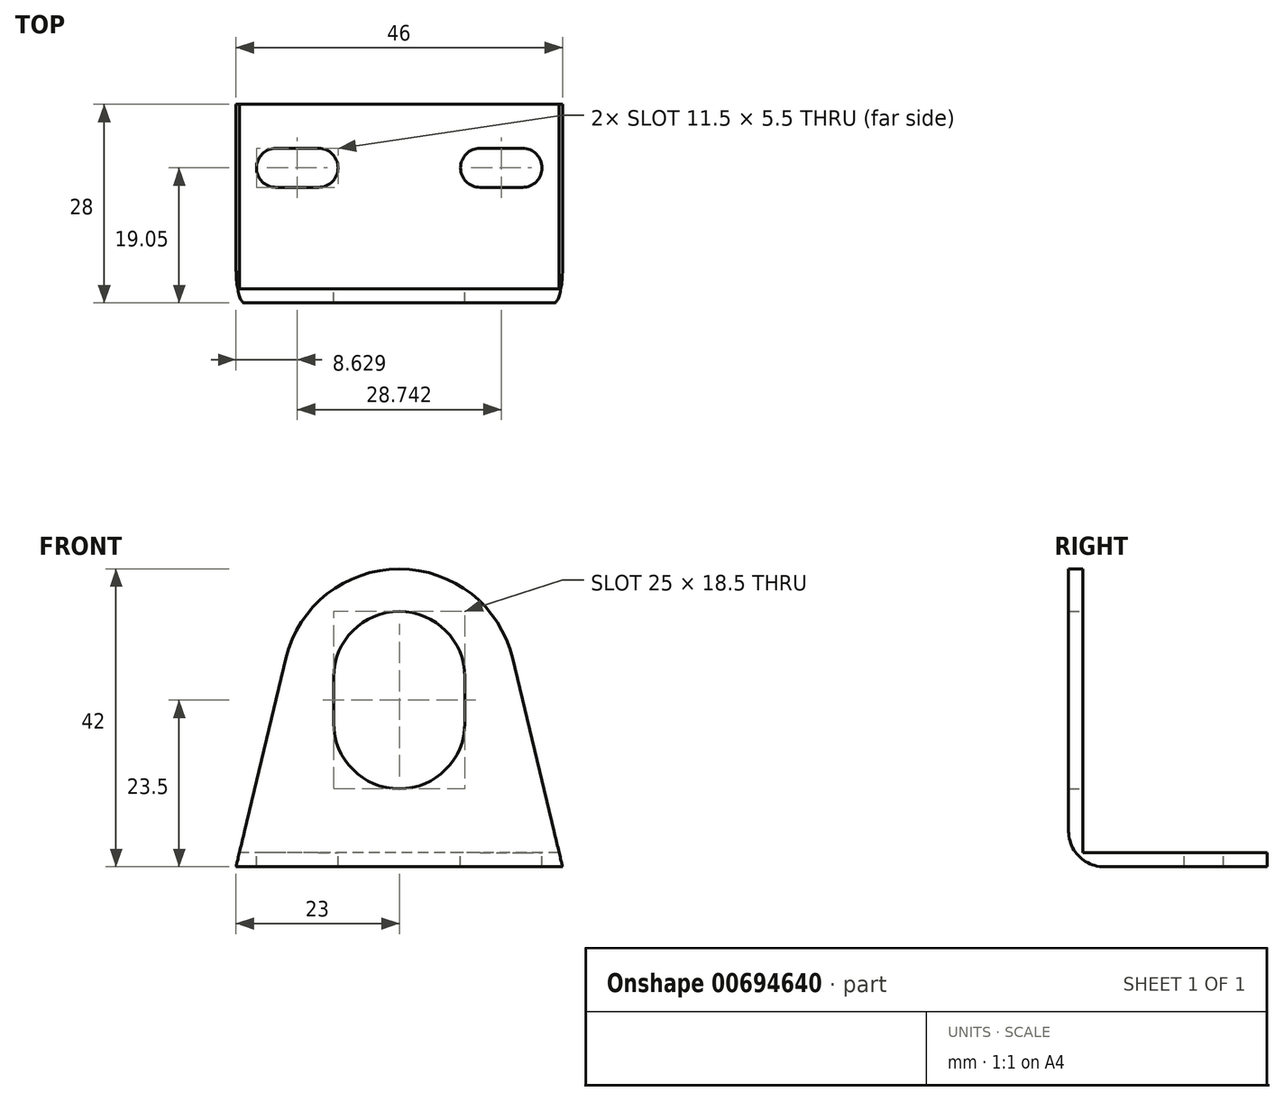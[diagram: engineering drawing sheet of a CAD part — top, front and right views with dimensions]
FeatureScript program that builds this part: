
annotation { "Feature Type Name" : "Feature", "Feature Type Description" : "" }
export const myFeature = defineFeature(function(context is Context, id is Id, definition is map)
    precondition{}
    {
        {
            var Q0;
            Q0=qCreatedBy(makeId("Front.planeOp"),FACE);
            var sketch = newSketch(context, id + "F0", { "sketchPlane" : qUnion([Q0])});
            skLineSegment(sketch, "E0", {"start": v(-23, 0) * mm, "end": v(23, 0) * mm});
            skLineSegment(sketch, "E1", {"start": v(23, 0) * mm, "end": v(15.96, 29.41) * mm});
            skLineSegment(sketch, "E2", {"start": v(-23, 0) * mm, "end": v(-15.96, 29.41) * mm});
            skArc(sketch, "E3", {"start": v(15.96, 29.41) * mm, "mid": v(0, 42) * mm, "end": v(-15.96, 29.41) * mm});
            skLineSegment(sketch, "E4", {"start": v(-9.25, 26.75) * mm, "end": v(-9.25, 20.25) * mm});
            skLineSegment(sketch, "E5", {"start": v(9.25, 26.75) * mm, "end": v(9.25, 20.25) * mm});
            skArc(sketch, "E6", {"start": v(-9.25, 20.25) * mm, "mid": v(0, 11) * mm, "end": v(9.25, 20.25) * mm});
            skArc(sketch, "E7", {"start": v(9.25, 26.75) * mm, "mid": v(0, 36) * mm, "end": v(-9.25, 26.75) * mm});
            skPoint(sketch, "E8", {"position": v(0, 0) * mm});
            skPoint(sketch, "E9", {"position": v(0, 42) * mm});
            skSolve(sketch);
        }
        {
            var Q0;
            Q0=qSketchRegion(id+"F0",true);
            extrude(context, id + "F1", {"entities" : qUnion([Q0]), "depth" : 2 * mm, "offsetDistance" : 25 * mm});
        }
        {
            var Q0;
            Q0=makeQuery(id+"F1.opExtrude","CAP_FACE",FACE,{"disambiguationData":[OSD([sQuery(id+"F0.wireOp",EDGE,"E0"),sQuery(id+"F0.wireOp",EDGE,"E1"),sQuery(id+"F0.wireOp",EDGE,"E2"),sQuery(id+"F0.wireOp",EDGE,"E3"),sQuery(id+"F0.wireOp",EDGE,"E4"),sQuery(id+"F0.wireOp",EDGE,"E5"),sQuery(id+"F0.wireOp",EDGE,"E6"),sQuery(id+"F0.wireOp",EDGE,"E7")])],"isStart":true});
            var sketch = newSketch(context, id + "F2", { "sketchPlane" : qUnion([Q0])});
            skLineSegment(sketch, "E10", {"start": v(-22.52, 2) * mm, "end": v(22.52, 2) * mm});
            skSolve(sketch);
        }
        {
            var Q0;
            {var subQ0=sQuery(id+"F2.wireOp",EDGE,"E10");Q0=makeQuery(id+"F2.imprint","IMPRINT",FACE,{"disambiguationData":[TD([[makeQuery(id+"F2.imprint","IMPRINT",EDGE,{"derivedFrom":subQ0}),-1.0]])]});}
            extrude(context, id + "F3", {"entities" : qUnion([Q0]), "operationType" : NewBodyOperationType.ADD, "depth" : 26 * mm, "offsetDistance" : 25 * mm});
        }
        {
            var Q0;
            Q0=makeQuery(id+"F1.opExtrude","CAP_EDGE",EDGE,{"disambiguationData":[OSD([sQuery(id+"F0.wireOp",EDGE,"E0")])],"isStart":false});
            var Q1;
            Q1=makeQuery(id+"F3.opExtrude","CAP_EDGE",EDGE,{"disambiguationData":[OSD([sQuery(id+"F2.wireOp",EDGE,"E10")])],"isStart":true});
            fillet(context, id + "F4", {"entities" : qUnion([Q0, Q1]), "radius" : 5 * mm, "tangentPropagation" : true, "allowEdgeOverflow" : false});
        }
        {
            var Q0;
            Q0=makeQuery(id+"F3.opExtrude","SWEPT_FACE",FACE,{"disambiguationData":[OSD([sQuery(id+"F2.wireOp",EDGE,"E10")])]});
            var sketch = newSketch(context, id + "F5", { "sketchPlane" : qUnion([Q0])});
            skLineSegment(sketch, "E11.bottom", {"start": v(11.37, 19.8) * mm, "end": v(17.37, 19.8) * mm});
            skLineSegment(sketch, "E11.top", {"start": v(11.37, 14.3) * mm, "end": v(17.37, 14.3) * mm});
            skLineSegment(sketch, "E12", {"start": v(0, 26) * mm, "end": v(0, 5) * mm, "construction": true});
            skArc(sketch, "E13", {"start": v(17.37, 14.3) * mm, "mid": v(20.12, 17.05) * mm, "end": v(17.37, 19.8) * mm});
            skArc(sketch, "E14", {"start": v(11.37, 19.8) * mm, "mid": v(8.62, 17.05) * mm, "end": v(11.37, 14.3) * mm});
            skLineSegment(sketch, "E15.MirrorCS", {"start": v(-11.37, 14.3) * mm, "end": v(-17.37, 14.3) * mm});
            skLineSegment(sketch, "E16.MirrorCS", {"start": v(-11.37, 19.8) * mm, "end": v(-17.37, 19.8) * mm});
            skArc(sketch, "E17.MirrorCS", {"start": v(-17.37, 14.3) * mm, "mid": v(-20.12, 17.05) * mm, "end": v(-17.37, 19.8) * mm});
            skArc(sketch, "E18.MirrorCS", {"start": v(-11.37, 19.8) * mm, "mid": v(-8.62, 17.05) * mm, "end": v(-11.37, 14.3) * mm});
            skSolve(sketch);
        }
        {
            var Q0;
            Q0=qSketchRegion(id+"F5",true);
            extrude(context, id + "F6", {"entities" : qUnion([Q0]), "operationType" : NewBodyOperationType.REMOVE, "endBound" : BoundingType.THROUGH_ALL, "oppositeDirection" : true, "depth" : 25 * mm, "offsetDistance" : 25 * mm});
        }
    });
